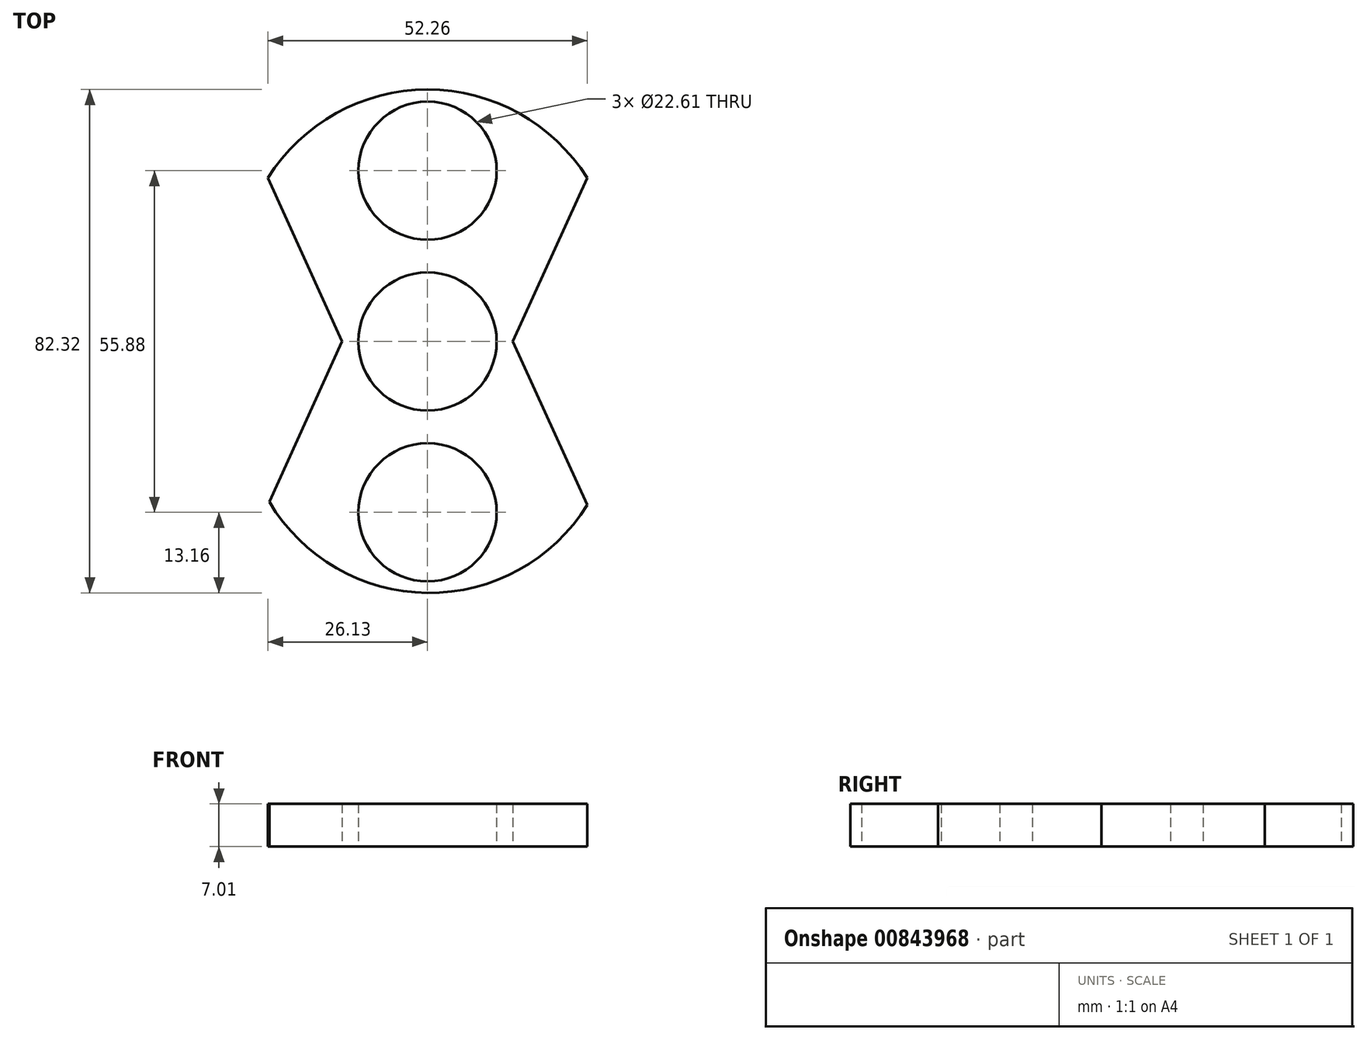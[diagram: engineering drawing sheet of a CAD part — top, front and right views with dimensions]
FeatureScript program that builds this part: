
annotation { "Feature Type Name" : "Feature", "Feature Type Description" : "" }
export const myFeature = defineFeature(function(context is Context, id is Id, definition is map)
    precondition{}
    {
        {
            var Q0;
            Q0=qCreatedBy(makeId("Top.planeOp"),FACE);
            var sketch = newSketch(context, id + "F0", { "sketchPlane" : qUnion([Q0])});
            skCircle(sketch, "E0", {"center": v(0, 0) * mm, "radius": 13.97 * mm});
            skCircle(sketch, "E1", {"center": v(0, 0) * mm, "radius": 11.3 * mm});
            skCircle(sketch, "E2", {"center": v(0, 27.94) * mm, "radius": 13.34 * mm});
            skCircle(sketch, "E3", {"center": v(0, -27.94) * mm, "radius": 13.34 * mm});
            skArc(sketch, "E4", {"start": v(-8.44, 11.13) * mm, "mid": v(-7.17, 14.38) * mm, "end": v(-8.46, 17.63) * mm});
            skArc(sketch, "E5", {"start": v(8.46, 17.63) * mm, "mid": v(7.02, 14.38) * mm, "end": v(8.44, 11.13) * mm});
            skArc(sketch, "E6", {"start": v(-8.44, -17.62) * mm, "mid": v(-7.1, -14.37) * mm, "end": v(-8.44, -11.13) * mm});
            skArc(sketch, "E7", {"start": v(8.44, -11.13) * mm, "mid": v(7.08, -14.37) * mm, "end": v(8.44, -17.62) * mm});
            skCircle(sketch, "E8", {"center": v(0, -27.94) * mm, "radius": 11.3 * mm});
            skCircle(sketch, "E9", {"center": v(0, 27.94) * mm, "radius": 11.3 * mm});
            skPoint(sketch, "E10", {"position": v(-8.97, 37.8) * mm});
            skPoint(sketch, "E11", {"position": v(-26.13, 26.73) * mm});
            skPoint(sketch, "E12", {"position": v(-12.64, 23.7) * mm});
            skPoint(sketch, "E13", {"position": v(26.13, 26.73) * mm});
            skPoint(sketch, "E14", {"position": v(12.64, 23.7) * mm});
            skPoint(sketch, "E15", {"position": v(8.97, 37.8) * mm});
            skPoint(sketch, "E16", {"position": v(13.97, 0) * mm});
            skPoint(sketch, "E17", {"position": v(-13.97, 0) * mm});
            skLineSegment(sketch, "E18", {"start": v(-26.13, 26.73) * mm, "end": v(-13.97, 0) * mm});
            skLineSegment(sketch, "E19", {"start": v(-26.13, -26.73) * mm, "end": v(-13.97, 0) * mm});
            skLineSegment(sketch, "E20", {"start": v(26.13, 26.73) * mm, "end": v(13.97, 0) * mm});
            skLineSegment(sketch, "E21", {"start": v(13.97, 0) * mm, "end": v(26.13, -26.73) * mm});
            skPoint(sketch, "E22", {"position": v(0.02, 41.27) * mm});
            skPoint(sketch, "E23", {"position": v(0, -41.28) * mm});
            skArc(sketch, "E24", {"start": v(26.13, 26.73) * mm, "mid": v(0, 41.22) * mm, "end": v(-26.13, 26.73) * mm});
            skArc(sketch, "E25", {"start": v(-25.9, -26.22) * mm, "mid": v(-0.03, -41.1) * mm, "end": v(26.13, -26.73) * mm});
            skSolve(sketch);
        }
        {
            var Q0;
            Q0=makeQuery(id+"F0.imprint","IMPRINT",FACE,{"disambiguationData":[TD([[makeQuery(id+"F0.imprint","IMPRINT",EDGE,{"derivedFrom":sQuery(id+"F0.wireOp",EDGE,"E9")}),-1.0]])]});
            var Q1;
            {var subQ0=sQuery(id+"F0.wireOp",EDGE,"38Mo33Jj-TySJ-Yn7Q-on5v-rEMiwyBiVKwd");Q1=makeQuery(id+"F0.imprint","IMPRINT",FACE,{"disambiguationData":[TD([[makeQuery(id+"F0.imprint","IMPRINT",EDGE,{"derivedFrom":subQ0}),1.0]])]});}
            var Q2;
            {var subQ0=sQuery(id+"F0.wireOp",EDGE,"E4");Q2=makeQuery(id+"F0.imprint","IMPRINT",FACE,{"disambiguationData":[TD([[makeQuery(id+"F0.imprint","IMPRINT",EDGE,{"derivedFrom":subQ0}),-1.0]])]});}
            var Q3;
            {var subQ0=sQuery(id+"F0.wireOp",EDGE,"E0");var subQ4=makeQuery(id+"F0.imprint","INTERSECT",VERTEX,{"derivedFrom":[subQ0,sQuery(id+"F0.wireOp",EDGE,"E4")]});Q3=makeQuery(id+"F0.imprint","IMPRINT",FACE,{"disambiguationData":[TD([[makeQuery(id+"F0.imprint","IMPRINT",EDGE,{"disambiguationData":[TD([[subQ4,1.0]])],"derivedFrom":subQ0}),1.0]])]});}
            var Q4;
            {var subQ5=sQuery(id+"F0.wireOp",EDGE,"E0");var subQ8=makeQuery(id+"F0.imprint","INTERSECT",VERTEX,{"derivedFrom":[subQ5,sQuery(id+"F0.wireOp",EDGE,"E5")]});Q4=makeQuery(id+"F0.imprint","IMPRINT",FACE,{"disambiguationData":[TD([[makeQuery(id+"F0.imprint","IMPRINT",EDGE,{"disambiguationData":[TD([[subQ8,-1.0]])],"derivedFrom":subQ5}),1.0]])]});}
            var Q5;
            {var subQ0=sQuery(id+"F0.wireOp",EDGE,"E5");Q5=makeQuery(id+"F0.imprint","IMPRINT",FACE,{"disambiguationData":[TD([[makeQuery(id+"F0.imprint","IMPRINT",EDGE,{"derivedFrom":subQ0}),-1.0]])]});}
            var Q6;
            {var subQ0=sQuery(id+"F0.wireOp",EDGE,"E7");Q6=makeQuery(id+"F0.imprint","IMPRINT",FACE,{"disambiguationData":[TD([[makeQuery(id+"F0.imprint","IMPRINT",EDGE,{"derivedFrom":subQ0}),-1.0]])]});}
            var Q7;
            {var subQ0=sQuery(id+"F0.wireOp",EDGE,"E6");Q7=makeQuery(id+"F0.imprint","IMPRINT",FACE,{"disambiguationData":[TD([[makeQuery(id+"F0.imprint","IMPRINT",EDGE,{"derivedFrom":subQ0}),-1.0]])]});}
            var Q8;
            Q8=makeQuery(id+"F0.imprint","IMPRINT",FACE,{"disambiguationData":[TD([[makeQuery(id+"F0.imprint","IMPRINT",EDGE,{"derivedFrom":sQuery(id+"F0.wireOp",EDGE,"E8")}),-1.0]])]});
            var Q9;
            {var subQ0=sQuery(id+"F0.wireOp",EDGE,"db898f4e-9596-438c-a1a4-356897919f26.2.0");Q9=makeQuery(id+"F0.imprint","IMPRINT",FACE,{"disambiguationData":[TD([[makeQuery(id+"F0.imprint","IMPRINT",EDGE,{"derivedFrom":subQ0}),1.0]])]});}
            var Q10;
            {var subQ0=sQuery(id+"F0.wireOp",EDGE,"6dqY5qWN-5gEB-a96H-pXmm-hYEs7Y3ciUDr");Q10=makeQuery(id+"F0.imprint","IMPRINT",FACE,{"disambiguationData":[TD([[makeQuery(id+"F0.imprint","IMPRINT",EDGE,{"derivedFrom":subQ0}),1.0]])]});}
            var Q11;
            {var subQ0=sQuery(id+"F0.wireOp",EDGE,"b6c16c0a-6696-430e-9aac-4465360cf5b5.2.0");Q11=makeQuery(id+"F0.imprint","IMPRINT",FACE,{"disambiguationData":[TD([[makeQuery(id+"F0.imprint","IMPRINT",EDGE,{"derivedFrom":subQ0}),1.0]])]});}
            var Q12;
            {var subQ1=sQuery(id+"F0.wireOp",EDGE,"E4");Q12=makeQuery(id+"F0.imprint","IMPRINT",FACE,{"disambiguationData":[TD([[makeQuery(id+"F0.imprint","IMPRINT",EDGE,{"derivedFrom":subQ1}),1.0]])]});}
            var Q13;
            {var subQ0=sQuery(id+"F0.wireOp",EDGE,"E5");Q13=makeQuery(id+"F0.imprint","IMPRINT",FACE,{"disambiguationData":[TD([[makeQuery(id+"F0.imprint","IMPRINT",EDGE,{"derivedFrom":subQ0}),1.0]])]});}
            var Q14;
            {var subQ0=sQuery(id+"F0.wireOp",EDGE,"E7");Q14=makeQuery(id+"F0.imprint","IMPRINT",FACE,{"disambiguationData":[TD([[makeQuery(id+"F0.imprint","IMPRINT",EDGE,{"derivedFrom":subQ0}),1.0]])]});}
            var Q15;
            {var subQ1=sQuery(id+"F0.wireOp",EDGE,"E6");Q15=makeQuery(id+"F0.imprint","IMPRINT",FACE,{"disambiguationData":[TD([[makeQuery(id+"F0.imprint","IMPRINT",EDGE,{"derivedFrom":subQ1}),1.0]])]});}
            var Q16;
            {var subQ0=sQuery(id+"F0.wireOp",EDGE,"fEm2spoK-7J6d-LKWQ-c3l1-HVo7nE1Mopu6");Q16=makeQuery(id+"F0.imprint","IMPRINT",FACE,{"disambiguationData":[TD([[makeQuery(id+"F0.imprint","IMPRINT",EDGE,{"derivedFrom":subQ0}),-1.0]])]});}
            var Q17;
            {var subQ0=sQuery(id+"F0.wireOp",EDGE,"yciKcqL1-Wm5z-eN3n-E9Ip-Zy0hjSFqY8Fa");Q17=makeQuery(id+"F0.imprint","IMPRINT",FACE,{"disambiguationData":[TD([[makeQuery(id+"F0.imprint","IMPRINT",EDGE,{"derivedFrom":subQ0}),-1.0]])]});}
            var Q18;
            {var subQ0=sQuery(id+"F0.wireOp",EDGE,"b6c16c0a-6696-430e-9aac-4465360cf5b5.2.1");Q18=makeQuery(id+"F0.imprint","IMPRINT",FACE,{"disambiguationData":[TD([[makeQuery(id+"F0.imprint","IMPRINT",EDGE,{"derivedFrom":subQ0}),-1.0]])]});}
            var Q19;
            {var subQ0=sQuery(id+"F0.wireOp",EDGE,"db898f4e-9596-438c-a1a4-356897919f26.2.1");Q19=makeQuery(id+"F0.imprint","IMPRINT",FACE,{"disambiguationData":[TD([[makeQuery(id+"F0.imprint","IMPRINT",EDGE,{"derivedFrom":subQ0}),-1.0]])]});}
            extrude(context, id + "F1", {"entities" : qUnion([Q0, Q1, Q2, Q3, Q4, Q5, Q6, Q7, Q8, Q9, Q10, Q11, Q12, Q13, Q14, Q15, Q16, Q17, Q18, Q19]), "depth" : 7 * mm, "offsetDistance" : 25.4 * mm});
        }
    });
